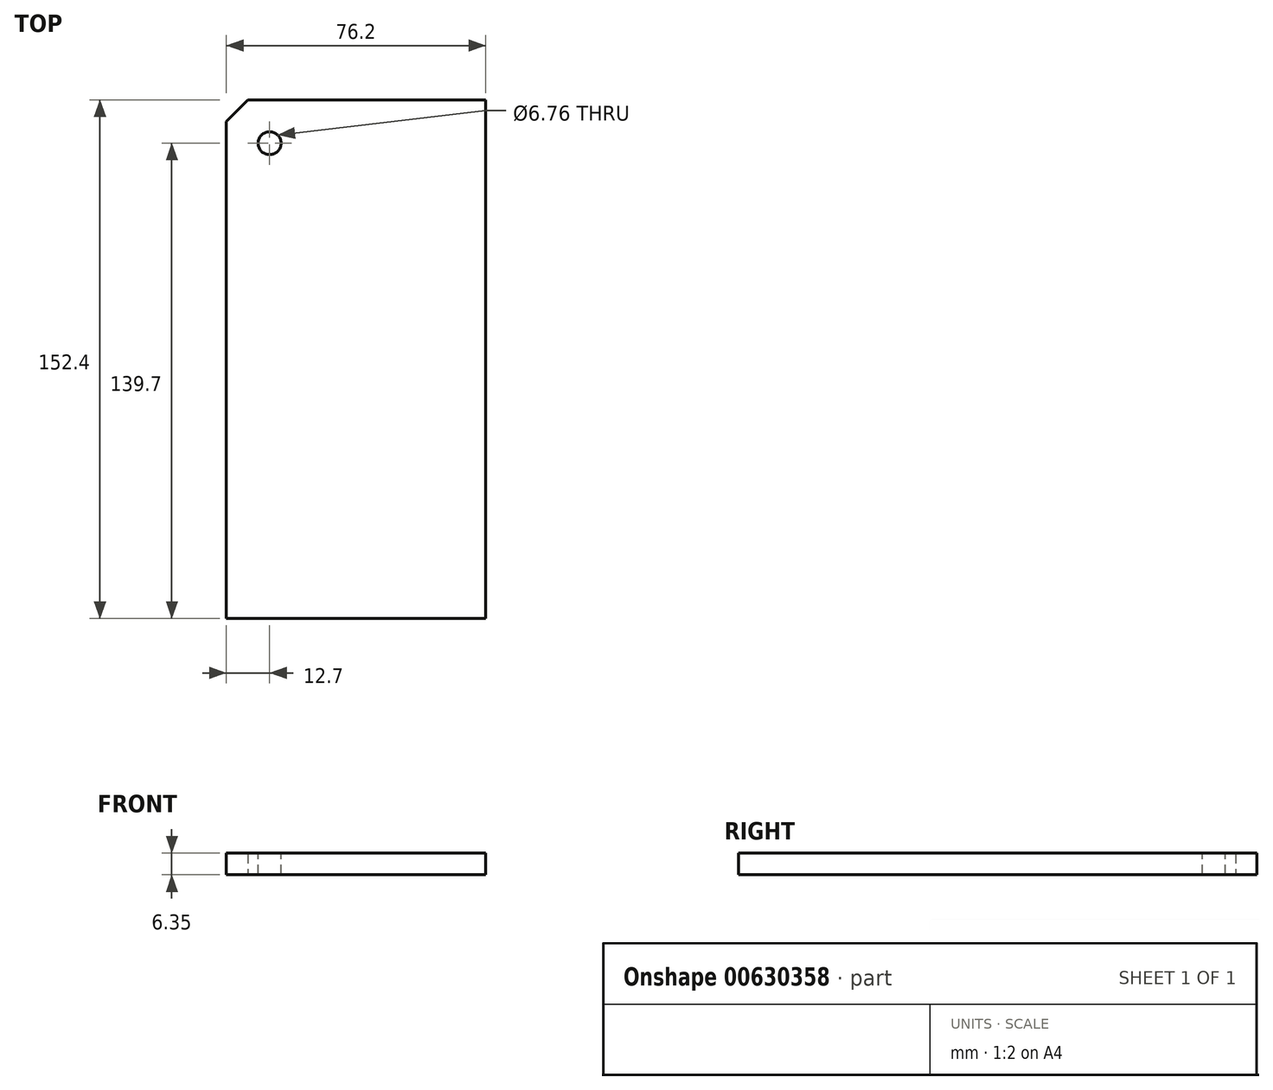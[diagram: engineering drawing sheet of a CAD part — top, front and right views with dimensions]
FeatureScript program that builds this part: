
annotation { "Feature Type Name" : "Feature", "Feature Type Description" : "" }
export const myFeature = defineFeature(function(context is Context, id is Id, definition is map)
    precondition{}
    {
        {
            var Q0;
            Q0=qCreatedBy(makeId("Top.planeOp"),FACE);
            var sketch = newSketch(context, id + "F0", { "sketchPlane" : qUnion([Q0])});
            skLineSegment(sketch, "E0.bottom", {"start": v(-31.81, 76.2) * mm, "end": v(38.1, 76.2) * mm});
            skLineSegment(sketch, "E0.top", {"start": v(-38.1, -76.2) * mm, "end": v(38.1, -76.2) * mm});
            skLineSegment(sketch, "E0.left", {"start": v(-38.1, 69.91) * mm, "end": v(-38.1, -76.2) * mm});
            skLineSegment(sketch, "E0.right", {"start": v(38.1, 76.2) * mm, "end": v(38.1, -76.2) * mm});
            skPoint(sketch, "E0.middle", {"position": v(0, 0) * mm});
            skLineSegment(sketch, "E1", {"start": v(-38.1, 69.91) * mm, "end": v(-31.81, 76.2) * mm});
            skLineSegment(sketch, "E2", {"start": v(0, -76.2) * mm, "end": v(0, 76.2) * mm, "construction": true});
            skSolve(sketch);
        }
        {
            var Q0;
            Q0 = qSketchRegion(id + "F0", true);
            extrude(context, id + "F1", {"entities" : qUnion([Q0]), "depth" : 6.35 * mm, "offsetDistance" : 25.4 * mm});
        }
        {
            var Q0;
            Q0=makeQuery(id+"F1.opExtrude","CAP_FACE",FACE,{"disambiguationData":[OSD([sQuery(id+"F0.wireOp",EDGE,"E0.bottom"),sQuery(id+"F0.wireOp",EDGE,"E0.top"),sQuery(id+"F0.wireOp",EDGE,"E0.left"),sQuery(id+"F0.wireOp",EDGE,"E0.right"),sQuery(id+"F0.wireOp",EDGE,"E1")])],"isStart":false});
            var sketch = newSketch(context, id + "F2", { "sketchPlane" : qUnion([Q0])});
            skLineSegment(sketch, "E3", {"start": v(-38.1, 63.5) * mm, "end": v(-25.4, 63.5) * mm, "construction": true});
            skLineSegment(sketch, "E4", {"start": v(-25.4, 63.5) * mm, "end": v(-25.4, 76.2) * mm, "construction": true});
            skPoint(sketch, "E5", {"position": v(-25.4, 63.5) * mm});
            skSolve(sketch);
        }
        {
            var Q0;
            Q0=sQuery(id+"F2.wireOp",VERTEX,"E5");
            var Q1;
            Q1=makeQuery(id+"F1.opExtrude","SWEPT_BODY",BODY,{"disambiguationData":[OSD([sQuery(id+"F0.wireOp",EDGE,"E0.bottom"),sQuery(id+"F0.wireOp",EDGE,"E0.top"),sQuery(id+"F0.wireOp",EDGE,"E0.left"),sQuery(id+"F0.wireOp",EDGE,"E0.right"),sQuery(id+"F0.wireOp",EDGE,"E1")])]});
            hole(context, id + "F3", {"style" : HoleStyle.SIMPLE, "endStyle" : HoleEndStyle.THROUGH, "standardTappedOrClearance" : lookupTablePath({ "standard" : "ANSI", "fit" : "Normal (ASME)", "size" : "1/4", "type" : "Clearance" }), "standardBlindInLast" : lookupTablePath({ "fit" : "Free", "standard" : "ANSI", "size" : "1/4", "type" : "Clearance" }), "holeDiameter" : 6.76 * mm, "majorDiameter" : 6.35 * mm, "isTappedThrough" : true, "tappedDepth" : 12.7 * mm, "tapClearance" : 3, "locations" : qUnion([Q0]), "scope" : qUnion([Q1])});
        }
    });
